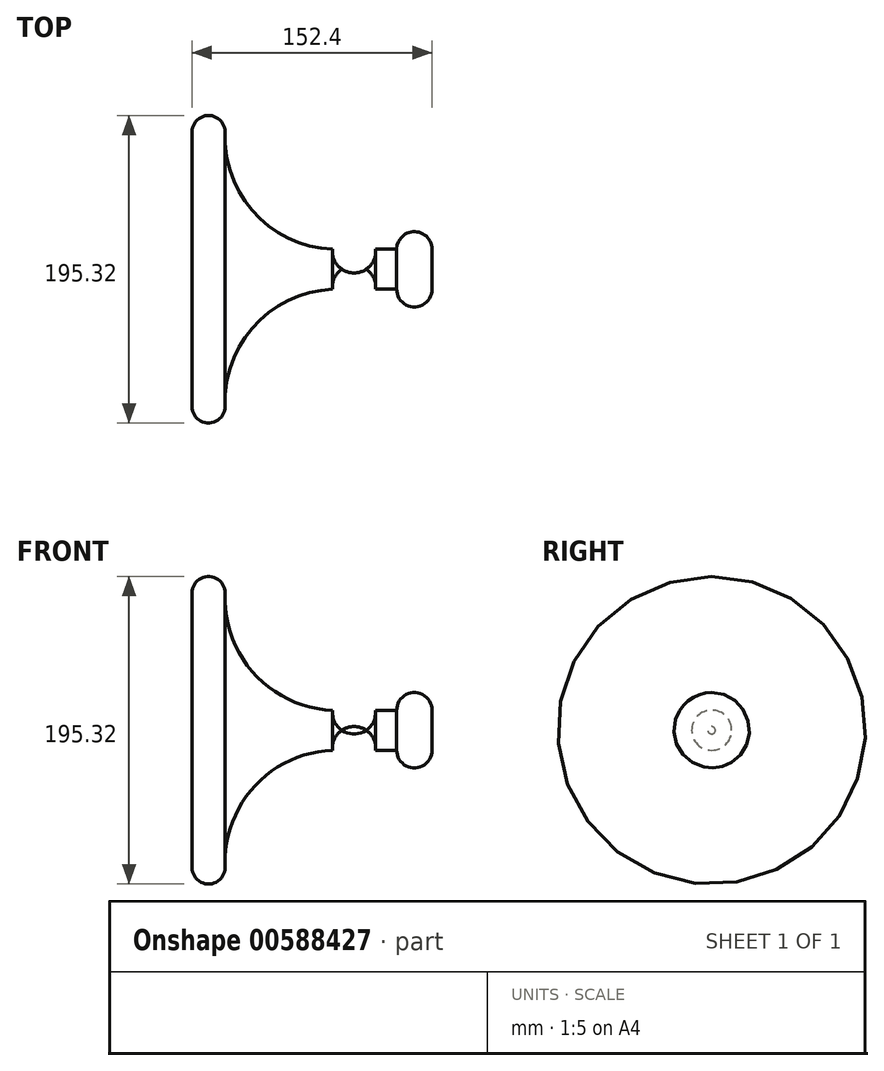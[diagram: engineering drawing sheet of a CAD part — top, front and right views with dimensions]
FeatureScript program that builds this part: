
annotation { "Feature Type Name" : "Feature", "Feature Type Description" : "" }
export const myFeature = defineFeature(function(context is Context, id is Id, definition is map)
    precondition{}
    {
        {
            var Q0;
            Q0=qCreatedBy(makeId("Front.planeOp"),FACE);
            var sketch = newSketch(context, id + "F0", { "sketchPlane" : qUnion([Q0])});
            skLineSegment(sketch, "E0", {"start": v(-125.03, 0) * mm, "end": v(27.37, 0) * mm});
            skLineSegment(sketch, "E1.bottom", {"start": v(-125.03, 0) * mm, "end": v(-125.03, 0) * mm});
            skLineSegment(sketch, "E1.top", {"start": v(-125.03, 87.15) * mm, "end": v(-125.03, 87.15) * mm});
            skLineSegment(sketch, "E1.left", {"start": v(-125.03, 0) * mm, "end": v(-125.03, 87.15) * mm});
            skLineSegment(sketch, "E1.right", {"start": v(-125.03, 0) * mm, "end": v(-125.03, 87.15) * mm});
            skArc(sketch, "E2", {"start": v(-125.03, 87.15) * mm, "mid": v(-114.3, 97.66) * mm, "end": v(-104, 86.71) * mm});
            skLineSegment(sketch, "E3", {"start": v(27.37, 0) * mm, "end": v(27.37, 12.7) * mm});
            skArc(sketch, "E4", {"start": v(27.37, 12.7) * mm, "mid": v(16.16, 23.91) * mm, "end": v(4.95, 12.7) * mm});
            skLineSegment(sketch, "E5", {"start": v(4.95, 12.7) * mm, "end": v(-8.39, 12.7) * mm});
            skArc(sketch, "E6", {"start": v(-8.39, 12.7) * mm, "mid": v(-22.12, 25.22) * mm, "end": v(-35.85, 12.7) * mm});
            skArc(sketch, "E7", {"start": v(-104, 86.71) * mm, "mid": v(-85.27, 35.58) * mm, "end": v(-35.85, 12.7) * mm});
            skSolve(sketch);
        }
        {
            var Q0;
            Q0=makeQuery(id+"F0.imprint","IMPRINT",FACE,{"disambiguationData":[TD([[makeQuery(id+"F0.imprint","IMPRINT",EDGE,{"derivedFrom":sQuery(id+"F0.wireOp",EDGE,"E0")}),1.0]])]});
            var Q1;
            Q1=sQuery(id+"F0.wireOp",EDGE,"E0");
            revolve(context, id + "F1", {"entities" : qUnion([Q0]), "axis" : qUnion([Q1]), "revolveType" : RevolveType.FULL});
        }
    });
